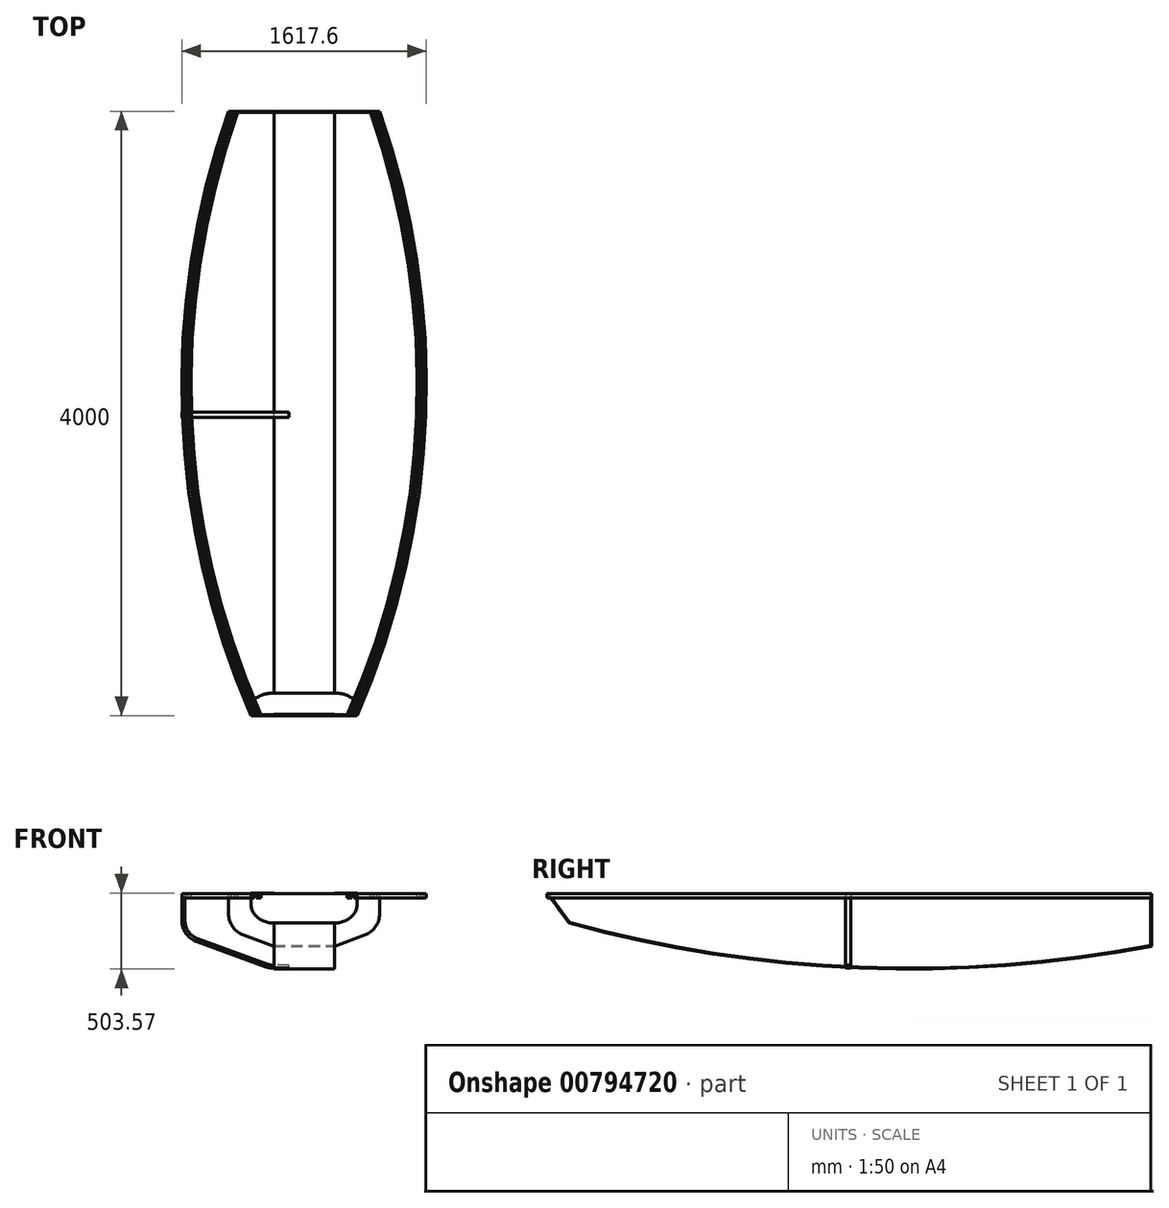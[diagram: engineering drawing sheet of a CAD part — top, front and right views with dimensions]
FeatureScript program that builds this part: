
annotation { "Feature Type Name" : "Feature", "Feature Type Description" : "" }
export const myFeature = defineFeature(function(context is Context, id is Id, definition is map)
    precondition{}
    {
        {
            var Q0;
            Q0=qCreatedBy(makeId("Right.planeOp"),FACE);
            var sketch = newSketch(context, id + "F0", { "sketchPlane" : qUnion([Q0])});
            skLineSegment(sketch, "E0.bottom", {"start": v(0, 0) * mm, "end": v(-4000, 0) * mm});
            skLineSegment(sketch, "E0.top", {"start": v(0, 500) * mm, "end": v(-4000, 500) * mm});
            skLineSegment(sketch, "E0.left", {"start": v(0, 0) * mm, "end": v(0, 500) * mm});
            skLineSegment(sketch, "E0.right", {"start": v(-4000, 0) * mm, "end": v(-4000, 500) * mm});
            skSolve(sketch);
        }
        {
            var Q0;
            Q0=qSketchRegion(id+"F0",true);
            extrude(context, id + "F1", {"entities" : qUnion([Q0]), "depth" : 200 * mm, "offsetDistance" : 25 * mm, "hasSecondDirection" : true, "secondDirectionOppositeDirection" : true, "secondDirectionDepth" : 200 * mm});
        }
        {
            var Q0;
            Q0=makeQuery(id+"F1.opExtrude","CAP_FACE",FACE,{"disambiguationData":[OSD([sQuery(id+"F0.wireOp",EDGE,"E0.bottom"),sQuery(id+"F0.wireOp",EDGE,"E0.top"),sQuery(id+"F0.wireOp",EDGE,"E0.left"),sQuery(id+"F0.wireOp",EDGE,"E0.right")])],"isStart":false});
            var sketch = newSketch(context, id + "F2", { "sketchPlane" : qUnion([Q0])});
            skLineSegment(sketch, "E1.0", {"start": v(0, 0) * mm, "end": v(-4000, 0) * mm});
            skLineSegment(sketch, "E2.0", {"start": v(0, 0) * mm, "end": v(0, 151.95) * mm});
            skArc(sketch, "E3", {"start": v(-3855.38, 304.68) * mm, "mid": v(-1936.47, 6.66) * mm, "end": v(0, 151.95) * mm});
            skPoint(sketch, "E4.orphan", {"position": v(0, 500) * mm});
            skPoint(sketch, "E5.orphan", {"position": v(-4121.15, 382.5) * mm});
            skPoint(sketch, "E6.start.orphan", {"position": v(-4000, 500) * mm});
            skLineSegment(sketch, "E7", {"start": v(-4000, 500) * mm, "end": v(-4000, 0) * mm});
            skLineSegment(sketch, "E8", {"start": v(-3855.38, 304.68) * mm, "end": v(-4000, 500) * mm});
            skSolve(sketch);
        }
        {
            var Q0;
            Q0=qSketchRegion(id+"F2",true);
            extrude(context, id + "F3", {"entities" : qUnion([Q0]), "operationType" : NewBodyOperationType.REMOVE, "endBound" : BoundingType.THROUGH_ALL, "oppositeDirection" : true, "depth" : 25 * mm, "offsetDistance" : 25 * mm});
        }
        {
            var Q0;
            Q0=makeQuery(id+"F1.opExtrude","CAP_FACE",FACE,{"disambiguationData":[OSD([sQuery(id+"F0.wireOp",EDGE,"E0.bottom"),sQuery(id+"F0.wireOp",EDGE,"E0.top"),sQuery(id+"F0.wireOp",EDGE,"E0.left"),sQuery(id+"F0.wireOp",EDGE,"E0.right")])],"isStart":false});
            var sketch = newSketch(context, id + "F4", { "sketchPlane" : qUnion([Q0])});
            skArc(sketch, "E9.0", {"start": v(-3851.8, 309.92) * mm, "mid": v(-1937.68, 12.71) * mm, "end": v(-6, 156.9) * mm});
            skLineSegment(sketch, "E10.0", {"start": v(-6, 156.9) * mm, "end": v(-6, 500) * mm});
            skLineSegment(sketch, "E11.0", {"start": v(-3851.8, 309.92) * mm, "end": v(-3992.53, 500) * mm});
            skLineSegment(sketch, "E12.0", {"start": v(-6, 500) * mm, "end": v(-3992.53, 500) * mm});
            skPoint(sketch, "E13.orphan", {"position": v(0, 500) * mm});
            skPoint(sketch, "E14.orphan", {"position": v(-4000, 500) * mm});
            skSolve(sketch);
        }
        {
            var Q0;
            Q0=qSketchRegion(id+"F4",true);
            extrude(context, id + "F5", {"entities" : qUnion([Q0]), "operationType" : NewBodyOperationType.REMOVE, "endBound" : BoundingType.THROUGH_ALL, "oppositeDirection" : true, "depth" : 25 * mm, "offsetDistance" : 25 * mm});
        }
        {
            var Q0;
            Q0=qCreatedBy(makeId("Front.planeOp"),FACE);
            cPlane(context, id + "F6", {"entities" : qUnion([Q0]), "cplaneType" : CPlaneType.OFFSET, "offset" : 200 * mm, "width" : 150 * mm, "height" : 150 * mm});
        }
        {
            var Q0;
            Q0=qCreatedBy(id+"F6.planeOp",FACE);
            cPlane(context, id + "F7", {"entities" : qUnion([Q0]), "cplaneType" : CPlaneType.OFFSET, "offset" : 200 * mm, "width" : 150 * mm, "height" : 150 * mm});
        }
        {
            var Q0;
            Q0=qCreatedBy(id+"F7.planeOp",FACE);
            cPlane(context, id + "F8", {"entities" : qUnion([Q0]), "cplaneType" : CPlaneType.OFFSET, "offset" : 200 * mm, "width" : 150 * mm, "height" : 150 * mm});
        }
        {
            var Q0;
            Q0=qCreatedBy(id+"F8.planeOp",FACE);
            cPlane(context, id + "F9", {"entities" : qUnion([Q0]), "cplaneType" : CPlaneType.OFFSET, "offset" : 200 * mm, "width" : 150 * mm, "height" : 150 * mm});
        }
        {
            var Q0;
            Q0=qCreatedBy(id+"F9.planeOp",FACE);
            cPlane(context, id + "F10", {"entities" : qUnion([Q0]), "cplaneType" : CPlaneType.OFFSET, "offset" : 200 * mm, "width" : 150 * mm, "height" : 150 * mm});
        }
        {
            var Q0;
            Q0=qCreatedBy(id+"F10.planeOp",FACE);
            cPlane(context, id + "F11", {"entities" : qUnion([Q0]), "cplaneType" : CPlaneType.OFFSET, "offset" : 200 * mm, "width" : 150 * mm, "height" : 150 * mm});
        }
        {
            var Q0;
            Q0=qCreatedBy(id+"F11.planeOp",FACE);
            cPlane(context, id + "F12", {"entities" : qUnion([Q0]), "cplaneType" : CPlaneType.OFFSET, "offset" : 200 * mm, "width" : 150 * mm, "height" : 150 * mm});
        }
        {
            var Q0;
            Q0=qCreatedBy(id+"F12.planeOp",FACE);
            cPlane(context, id + "F13", {"entities" : qUnion([Q0]), "cplaneType" : CPlaneType.OFFSET, "offset" : 200 * mm, "width" : 150 * mm, "height" : 150 * mm});
        }
        {
            var Q0;
            Q0=qCreatedBy(id+"F13.planeOp",FACE);
            cPlane(context, id + "F14", {"entities" : qUnion([Q0]), "cplaneType" : CPlaneType.OFFSET, "offset" : 200 * mm, "width" : 150 * mm, "height" : 150 * mm});
        }
        {
            var Q0;
            Q0=qCreatedBy(id+"F14.planeOp",FACE);
            cPlane(context, id + "F15", {"entities" : qUnion([Q0]), "cplaneType" : CPlaneType.OFFSET, "offset" : 200 * mm, "width" : 150 * mm, "height" : 150 * mm});
        }
        {
            var Q0;
            Q0=qCreatedBy(id+"F15.planeOp",FACE);
            cPlane(context, id + "F16", {"entities" : qUnion([Q0]), "cplaneType" : CPlaneType.OFFSET, "offset" : 200 * mm, "width" : 150 * mm, "height" : 150 * mm});
        }
        {
            var Q0;
            Q0=qCreatedBy(id+"F16.planeOp",FACE);
            cPlane(context, id + "F17", {"entities" : qUnion([Q0]), "cplaneType" : CPlaneType.OFFSET, "offset" : 200 * mm, "width" : 150 * mm, "height" : 150 * mm});
        }
        {
            var Q0;
            Q0=qCreatedBy(id+"F17.planeOp",FACE);
            cPlane(context, id + "F18", {"entities" : qUnion([Q0]), "cplaneType" : CPlaneType.OFFSET, "offset" : 200 * mm, "width" : 150 * mm, "height" : 150 * mm});
        }
        {
            var Q0;
            Q0=qCreatedBy(id+"F18.planeOp",FACE);
            cPlane(context, id + "F19", {"entities" : qUnion([Q0]), "cplaneType" : CPlaneType.OFFSET, "offset" : 200 * mm, "width" : 150 * mm, "height" : 150 * mm});
        }
        {
            var Q0;
            Q0=qCreatedBy(id+"F19.planeOp",FACE);
            cPlane(context, id + "F20", {"entities" : qUnion([Q0]), "cplaneType" : CPlaneType.OFFSET, "offset" : 200 * mm, "width" : 150 * mm, "height" : 150 * mm});
        }
        {
            var Q0;
            Q0=qCreatedBy(id+"F20.planeOp",FACE);
            cPlane(context, id + "F21", {"entities" : qUnion([Q0]), "cplaneType" : CPlaneType.OFFSET, "offset" : 200 * mm, "width" : 150 * mm, "height" : 150 * mm});
        }
        {
            var Q0;
            Q0=qCreatedBy(id+"F21.planeOp",FACE);
            cPlane(context, id + "F22", {"entities" : qUnion([Q0]), "cplaneType" : CPlaneType.OFFSET, "offset" : 200 * mm, "width" : 150 * mm, "height" : 150 * mm});
        }
        {
            var Q0;
            Q0=qCreatedBy(id+"F22.planeOp",FACE);
            cPlane(context, id + "F23", {"entities" : qUnion([Q0]), "cplaneType" : CPlaneType.OFFSET, "offset" : 200 * mm, "width" : 150 * mm, "height" : 150 * mm});
        }
        {
            var Q0;
            Q0=qCreatedBy(makeId("Top.planeOp"),FACE);
            cPlane(context, id + "F24", {"entities" : qUnion([Q0]), "cplaneType" : CPlaneType.OFFSET, "offset" : 500 * mm, "width" : 150 * mm, "height" : 150 * mm});
        }
        {
            var Q0;
            Q0=makeQuery(id+"F3.boolean.opBoolean","COPY",FACE,{"derivedFrom":makeQuery(id+"F3.opExtrude","SWEPT_FACE",FACE,{"disambiguationData":[OSD([sQuery(id+"F2.wireOp",EDGE,"E8")])]})});
            var sketch = newSketch(context, id + "F25", { "sketchPlane" : qUnion([Q0])});
            skLineSegment(sketch, "E15.0.3", {"start": v(200, 2539.04) * mm, "end": v(-200, 2539.04) * mm});
            skLineSegment(sketch, "E16.0", {"start": v(-200, 2539.04) * mm, "end": v(-200, 2782.07) * mm});
            skLineSegment(sketch, "E17", {"start": v(-200, 2782.07) * mm, "end": v(-350, 2782.07) * mm});
            skPoint(sketch, "E15.0.1.end.orphan", {"position": v(200, 122.12) * mm});
            skPoint(sketch, "E15.0.1.start.orphan", {"position": v(-200, 122.12) * mm});
            skArc(sketch, "E18", {"start": v(-200, 2539.04) * mm, "mid": v(-306.07, 2582.97) * mm, "end": v(-350, 2689.04) * mm});
            skLineSegment(sketch, "E19", {"start": v(-200, 2689.04) * mm, "end": v(-440.1, 2689.04) * mm, "construction": true});
            skLineSegment(sketch, "E20", {"start": v(-350, 2689.04) * mm, "end": v(-350, 2782.07) * mm});
            skSolve(sketch);
        }
        {
            var Q0;
            Q0=qSketchRegion(id+"F25",true);
            extrude(context, id + "F26", {"entities" : qUnion([Q0]), "oppositeDirection" : true, "depth" : 6 * mm, "offsetDistance" : 25 * mm});
        }
        {
            var Q0;
            Q0=makeQuery(id+"F26.opExtrude","SWEPT_BODY",BODY,{"disambiguationData":[OSD([sQuery(id+"F25.wireOp",EDGE,"E16.0"),sQuery(id+"F25.wireOp",EDGE,"E17"),sQuery(id+"F25.wireOp",EDGE,"E18"),sQuery(id+"F25.wireOp",EDGE,"E20")])]});
            var Q1;
            Q1=qCreatedBy(makeId("Right.planeOp"),FACE);
            mirror(context, id + "F27", {"operationType" : NewBodyOperationType.ADD, "entities" : qUnion([Q0]), "mirrorPlane" : qUnion([Q1])});
        }
        {
            var Q0;
            Q0=qCreatedBy(id+"F24.planeOp",FACE);
            var sketch = newSketch(context, id + "F28", { "sketchPlane" : qUnion([Q0])});
            skLineSegment(sketch, "E21", {"start": v(-436.36, 0) * mm, "end": v(-457.58, 0) * mm});
            skLineSegment(sketch, "E22", {"start": v(0, 0) * mm, "end": v(0, -4123.04) * mm, "construction": true});
            skLineSegment(sketch, "E23.0", {"start": v(-200, -4000) * mm, "end": v(-326.44, -4000) * mm, "construction": true});
            skLineSegment(sketch, "E24", {"start": v(0, -1500) * mm, "end": v(-800, -1500) * mm, "construction": true});
            skArc(sketch, "E25", {"start": v(-500, 0) * mm, "mid": v(-804.96, -2014.25) * mm, "end": v(-350, -4000) * mm});
            skArc(sketch, "E26.0", {"start": v(-478.8, 0) * mm, "mid": v(-682.4, -739.35) * mm, "end": v(-779.97, -1500) * mm});
            skArc(sketch, "E27.0", {"start": v(-457.58, 0) * mm, "mid": v(-764.93, -2014.48) * mm, "end": v(-306.3, -4000) * mm});
            skArc(sketch, "E28.0", {"start": v(-436.36, 0) * mm, "mid": v(-744.9, -2014.6) * mm, "end": v(-284.42, -4000) * mm});
            skLineSegment(sketch, "E29", {"start": v(-284.42, -4000) * mm, "end": v(-306.3, -4000) * mm});
            skLineSegment(sketch, "E30.trimOffspring", {"start": v(-478.8, 0) * mm, "end": v(-500, 0) * mm});
            skLineSegment(sketch, "E31", {"start": v(-350, -4000) * mm, "end": v(-326.44, -4000) * mm});
            skArc(sketch, "E32.0", {"start": v(-779.97, -1500) * mm, "mid": v(-702.12, -2776.76) * mm, "end": v(-328.16, -4000) * mm});
            skLineSegment(sketch, "E33.trimOffspring", {"start": v(-328.16, -4000) * mm, "end": v(-350, -4000) * mm, "construction": true});
            skSolve(sketch);
        }
        {
            var Q0;
            Q0=qSketchRegion(id+"F28",true);
            extrude(context, id + "F29", {"entities" : qUnion([Q0]), "oppositeDirection" : true, "depth" : 30 * mm, "offsetDistance" : 25 * mm});
        }
        {
            var Q0;
            Q0=makeQuery(id+"F29.opExtrude","SWEPT_BODY",BODY,{"disambiguationData":[OSD([sQuery(id+"F28.wireOp",EDGE,"E25"),sQuery(id+"F28.wireOp",EDGE,"E26.0"),sQuery(id+"F28.wireOp",EDGE,"JQv3v1hN-lLp6-lVGY-2l0k-aHUHcDUw9ejT"),sQuery(id+"F28.wireOp",EDGE,"E30.trimOffspring")])]});
            var Q1;
            Q1=makeQuery(id+"F29.opExtrude","SWEPT_BODY",BODY,{"disambiguationData":[OSD([sQuery(id+"F28.wireOp",EDGE,"E21"),sQuery(id+"F28.wireOp",EDGE,"E27.0"),sQuery(id+"F28.wireOp",EDGE,"E28.0"),sQuery(id+"F28.wireOp",EDGE,"E29")])]});
            var Q2;
            Q2=qCreatedBy(makeId("Right.planeOp"),FACE);
            mirror(context, id + "F30", {"operationType" : NewBodyOperationType.ADD, "entities" : qUnion([Q0, Q1]), "mirrorPlane" : qUnion([Q2])});
        }
        {
            var Q0;
            Q0=qCreatedBy(makeId("Front.planeOp"),FACE);
            var sketch = newSketch(context, id + "F31", { "sketchPlane" : qUnion([Q0])});
            skLineSegment(sketch, "E34.0", {"start": v(200, 151.95) * mm, "end": v(200, 500) * mm});
            skLineSegment(sketch, "E35.0", {"start": v(-200, 151.95) * mm, "end": v(200, 151.95) * mm, "construction": true});
            skLineSegment(sketch, "E36.0", {"start": v(500, 470) * mm, "end": v(500, 500) * mm});
            skLineSegment(sketch, "E37", {"start": v(500, 470) * mm, "end": v(500, 366.17) * mm});
            skLineSegment(sketch, "E38", {"start": v(500, 366.17) * mm, "end": v(350, 366.17) * mm, "construction": true});
            skArc(sketch, "E39", {"start": v(401.3, 225.21) * mm, "mid": v(472.87, 280.13) * mm, "end": v(500, 366.17) * mm});
            skLineSegment(sketch, "E40", {"start": v(200, 151.95) * mm, "end": v(401.3, 225.21) * mm});
            skLineSegment(sketch, "E41", {"start": v(500, 500) * mm, "end": v(200, 500) * mm});
            skSolve(sketch);
        }
        {
            var Q0;
            Q0=qSketchRegion(id+"F31",true);
            extrude(context, id + "F32", {"entities" : qUnion([Q0]), "depth" : 6 * mm, "offsetDistance" : 25 * mm});
        }
        {
            var Q0;
            Q0=makeQuery(id+"F32.opExtrude","SWEPT_BODY",BODY,{"disambiguationData":[OSD([sQuery(id+"F31.wireOp",EDGE,"E34.0"),sQuery(id+"F31.wireOp",EDGE,"E36.0"),sQuery(id+"F31.wireOp",EDGE,"E37"),sQuery(id+"F31.wireOp",EDGE,"E39"),sQuery(id+"F31.wireOp",EDGE,"E40"),sQuery(id+"F31.wireOp",EDGE,"E41")])]});
            var Q1;
            Q1=qCreatedBy(makeId("Right.planeOp"),FACE);
            mirror(context, id + "F33", {"operationType" : NewBodyOperationType.ADD, "entities" : qUnion([Q0]), "mirrorPlane" : qUnion([Q1])});
        }
        {
            var Q0;
            Q0=qCreatedBy(id+"F15.planeOp",FACE);
            var sketch = newSketch(context, id + "F34", { "sketchPlane" : qUnion([Q0])});
            skLineSegment(sketch, "E42", {"start": v(-100, 6) * mm, "end": v(-200, 6) * mm});
            skLineSegment(sketch, "E43", {"start": v(-100, 6) * mm, "end": v(-100, 26) * mm});
            skLineSegment(sketch, "E44.0", {"start": v(-100, 26) * mm, "end": v(-200, 26) * mm});
            skLineSegment(sketch, "E45", {"start": v(-200, 6) * mm, "end": v(-200, 156) * mm, "construction": true});
            skLineSegment(sketch, "E46", {"start": v(-200, 156) * mm, "end": v(-282.27, -70.04) * mm, "construction": true});
            skArc(sketch, "E47", {"start": v(-251.3, 15.05) * mm, "mid": v(-226.05, 8.28) * mm, "end": v(-200, 6) * mm});
            skArc(sketch, "E48.0", {"start": v(-244.46, 33.84) * mm, "mid": v(-222.57, 27.97) * mm, "end": v(-200, 26) * mm});
            skLineSegment(sketch, "E49", {"start": v(-808.8, 470) * mm, "end": v(-808.8, 500) * mm});
            skLineSegment(sketch, "E50", {"start": v(-808.8, 470) * mm, "end": v(-808.8, 322.99) * mm});
            skLineSegment(sketch, "E51.0", {"start": v(-788.8, 500) * mm, "end": v(-788.8, 297.72) * mm});
            skLineSegment(sketch, "E52", {"start": v(-808.8, 500) * mm, "end": v(-788.8, 500) * mm});
            skLineSegment(sketch, "E53", {"start": v(-808.8, 322.99) * mm, "end": v(-658.8, 322.99) * mm, "construction": true});
            skArc(sketch, "E54", {"start": v(-808.8, 322.99) * mm, "mid": v(-781.67, 236.95) * mm, "end": v(-710.1, 182.03) * mm});
            skLineSegment(sketch, "E55", {"start": v(-251.3, 15.05) * mm, "end": v(-710.1, 182.03) * mm});
            skArc(sketch, "E56.0", {"start": v(-788.8, 322.99) * mm, "mid": v(-765.29, 248.42) * mm, "end": v(-703.26, 200.83) * mm});
            skLineSegment(sketch, "E57.0", {"start": v(-244.46, 33.84) * mm, "end": v(-703.26, 200.83) * mm});
            skSolve(sketch);
        }
        {
            var Q0;
            Q0=qSketchRegion(id+"F34",true);
            extrude(context, id + "F35", {"entities" : qUnion([Q0]), "depth" : 25 * mm, "offsetDistance" : 25 * mm, "hasSecondDirection" : true, "secondDirectionOppositeDirection" : true, "secondDirectionDepth" : 10 * mm});
        }
    });
